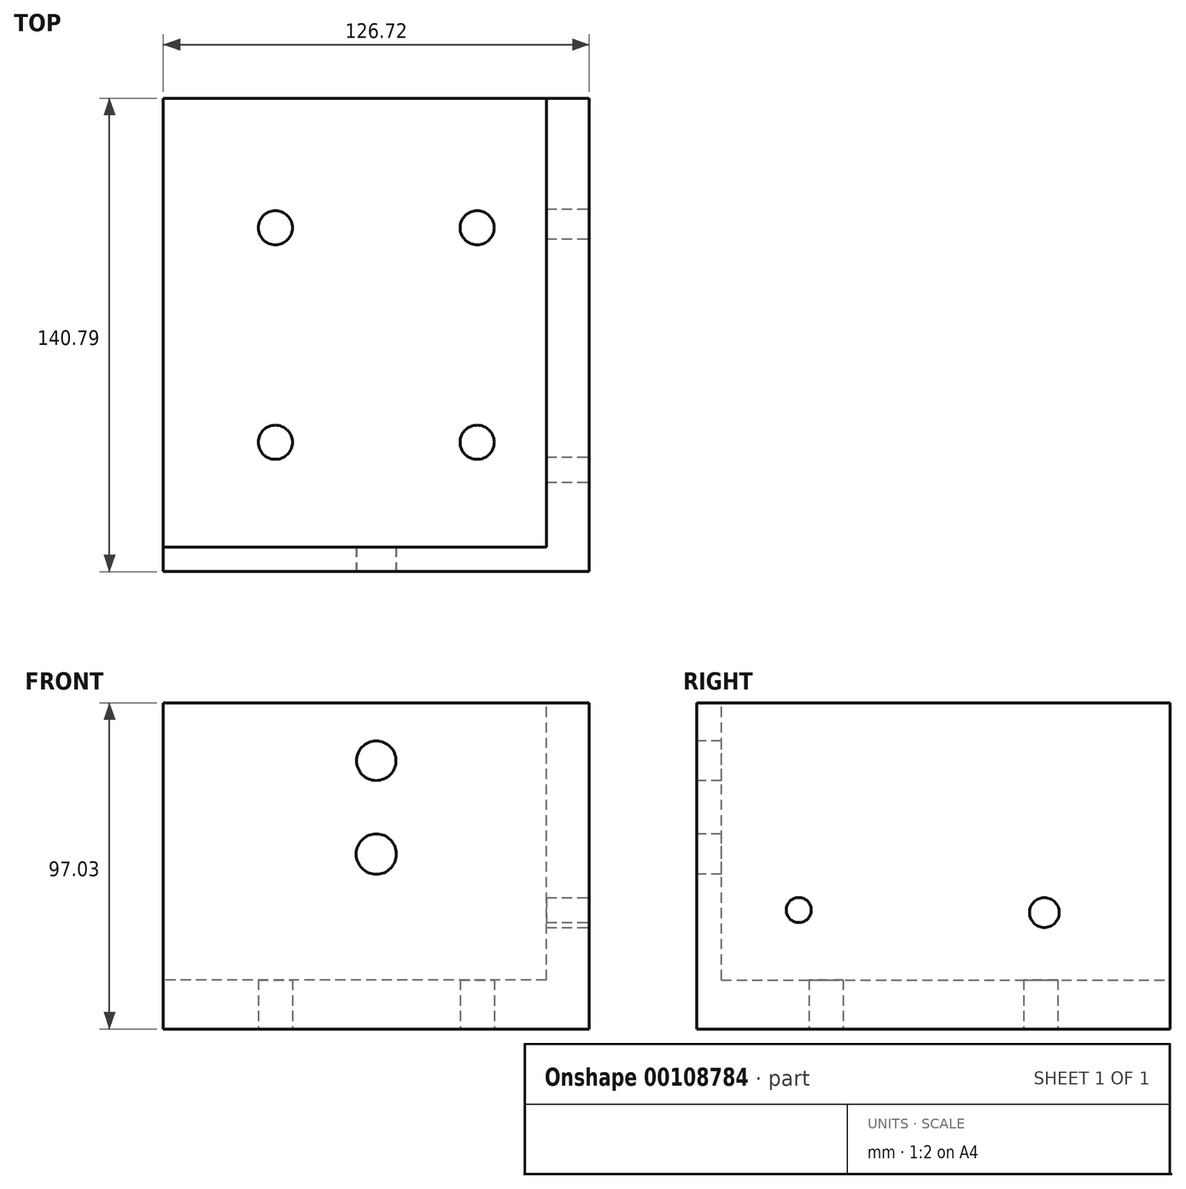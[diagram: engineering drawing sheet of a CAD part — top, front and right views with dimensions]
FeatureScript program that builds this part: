
annotation { "Feature Type Name" : "Feature", "Feature Type Description" : "" }
export const myFeature = defineFeature(function(context is Context, id is Id, definition is map)
    precondition{}
    {
        {
            var Q0;
            Q0=qCreatedBy(makeId("Front.planeOp"),FACE);
            var sketch = newSketch(context, id + "F0", { "sketchPlane" : qUnion([Q0])});
            skLineSegment(sketch, "E0.bottom", {"start": v(63.36, -7.3) * mm, "end": v(-63.36, -7.3) * mm});
            skLineSegment(sketch, "E0.top", {"start": v(63.36, 7.3) * mm, "end": v(-63.36, 7.3) * mm});
            skLineSegment(sketch, "E0.left", {"start": v(63.36, -7.3) * mm, "end": v(63.36, 7.3) * mm});
            skLineSegment(sketch, "E0.right", {"start": v(-63.36, -7.3) * mm, "end": v(-63.36, 7.3) * mm});
            skPoint(sketch, "E0.middle", {"position": v(0, 0) * mm});
            skLineSegment(sketch, "E1.bottom", {"start": v(-63.36, 7.3) * mm, "end": v(-50.64, 7.3) * mm});
            skLineSegment(sketch, "E1.top", {"start": v(-63.36, 89.74) * mm, "end": v(-50.64, 89.74) * mm});
            skLineSegment(sketch, "E1.left", {"start": v(-63.36, 7.3) * mm, "end": v(-63.36, 89.74) * mm});
            skLineSegment(sketch, "E1.right", {"start": v(-50.64, 7.3) * mm, "end": v(-50.64, 89.74) * mm});
            skLineSegment(sketch, "E2.MirrorCS", {"start": v(50.64, 7.3) * mm, "end": v(50.64, 89.74) * mm});
            skLineSegment(sketch, "E3.MirrorCS", {"start": v(63.36, 7.3) * mm, "end": v(50.64, 7.3) * mm});
            skLineSegment(sketch, "E4.MirrorCS", {"start": v(63.36, 7.3) * mm, "end": v(63.36, 89.74) * mm});
            skLineSegment(sketch, "E5.MirrorCS", {"start": v(63.36, 89.74) * mm, "end": v(50.64, 89.74) * mm});
            skSolve(sketch);
        }
        {
            var Q0;
            Q0=makeQuery(id+"F0.imprint","IMPRINT",FACE,{"disambiguationData":[TD([[makeQuery(id+"F0.imprint","IMPRINT",EDGE,{"derivedFrom":sQuery(id+"F0.wireOp",EDGE,"E1.bottom")}),1.0]])]});
            var Q1;
            Q1=makeQuery(id+"F0.imprint","IMPRINT",FACE,{"disambiguationData":[TD([[makeQuery(id+"F0.imprint","IMPRINT",EDGE,{"derivedFrom":sQuery(id+"F0.wireOp",EDGE,"E0.bottom")}),-1.0]])]});
            var Q2;
            Q2=makeQuery(id+"F0.imprint","IMPRINT",FACE,{"disambiguationData":[TD([[makeQuery(id+"F0.imprint","IMPRINT",EDGE,{"derivedFrom":sQuery(id+"F0.wireOp",EDGE,"E2.MirrorCS")}),-1.0]])]});
            extrude(context, id + "F1", {"entities" : qUnion([Q0, Q1, Q2]), "depth" : 140.79 * mm});
        }
        {
            var Q0;
            Q0=makeQuery(id+"F1.opExtrude","SWEPT_FACE",FACE,{"disambiguationData":[OSD([sQuery(id+"F0.wireOp",EDGE,"E0.left"),sQuery(id+"F0.wireOp",EDGE,"E4.MirrorCS")])]});
            var sketch = newSketch(context, id + "F2", { "sketchPlane" : qUnion([Q0])});
            skCircle(sketch, "E6", {"center": v(-110.43, 28.09) * mm, "radius": 3.72 * mm});
            skCircle(sketch, "E7", {"center": v(-37.36, 27.34) * mm, "radius": 4.43 * mm});
            skSolve(sketch);
        }
        {
            var Q0;
            Q0 = qSketchRegion(id + "F2", true);
            extrude(context, id + "F3", {"entities" : qUnion([Q0]), "operationType" : NewBodyOperationType.REMOVE, "oppositeDirection" : true, "depth" : 151.84 * mm});
        }
        {
            var Q0;
            Q0=makeQuery(id+"F1.opExtrude","CAP_FACE",FACE,{"disambiguationData":[OSD([sQuery(id+"F0.wireOp",EDGE,"E0.bottom"),sQuery(id+"F0.wireOp",EDGE,"E0.top"),sQuery(id+"F0.wireOp",EDGE,"E0.left"),sQuery(id+"F0.wireOp",EDGE,"E0.right"),sQuery(id+"F0.wireOp",EDGE,"E1.top"),sQuery(id+"F0.wireOp",EDGE,"E1.left"),sQuery(id+"F0.wireOp",EDGE,"E1.right"),sQuery(id+"F0.wireOp",EDGE,"E2.MirrorCS"),sQuery(id+"F0.wireOp",EDGE,"E4.MirrorCS"),sQuery(id+"F0.wireOp",EDGE,"E5.MirrorCS")])],"isStart":false});
            var sketch = newSketch(context, id + "F4", { "sketchPlane" : qUnion([Q0])});
            skLineSegment(sketch, "E8.bottom", {"start": v(-63.36, 89.74) * mm, "end": v(63.36, 89.74) * mm});
            skLineSegment(sketch, "E8.top", {"start": v(-63.36, -7.3) * mm, "end": v(63.36, -7.3) * mm});
            skLineSegment(sketch, "E8.left", {"start": v(-63.36, 89.74) * mm, "end": v(-63.36, -7.3) * mm});
            skLineSegment(sketch, "E8.right", {"start": v(63.36, 89.74) * mm, "end": v(63.36, -7.3) * mm});
            skSolve(sketch);
        }
        {
            var Q0;
            Q0 = qSketchRegion(id + "F4", true);
            extrude(context, id + "F5", {"entities" : qUnion([Q0]), "operationType" : NewBodyOperationType.ADD, "oppositeDirection" : true, "depth" : 7.33 * mm});
        }
        {
            var Q0;
            Q0=makeQuery(id+"F5.boolean.opBoolean","MERGE",FACE,{"derivedFrom":[makeQuery(id+"F1.opExtrude","CAP_FACE",FACE,{"disambiguationData":[OSD([sQuery(id+"F0.wireOp",EDGE,"E0.bottom"),sQuery(id+"F0.wireOp",EDGE,"E0.top"),sQuery(id+"F0.wireOp",EDGE,"E0.left"),sQuery(id+"F0.wireOp",EDGE,"E0.right"),sQuery(id+"F0.wireOp",EDGE,"E1.top"),sQuery(id+"F0.wireOp",EDGE,"E1.left"),sQuery(id+"F0.wireOp",EDGE,"E1.right"),sQuery(id+"F0.wireOp",EDGE,"E2.MirrorCS"),sQuery(id+"F0.wireOp",EDGE,"E4.MirrorCS"),sQuery(id+"F0.wireOp",EDGE,"E5.MirrorCS")])],"isStart":false}),makeQuery(id+"F5.opExtrude","CAP_FACE",FACE,{"disambiguationData":[OSD([sQuery(id+"F4.wireOp",EDGE,"E8.bottom"),sQuery(id+"F4.wireOp",EDGE,"E8.top"),sQuery(id+"F4.wireOp",EDGE,"E8.left"),sQuery(id+"F4.wireOp",EDGE,"E8.right")])],"isStart":true})]});
            var sketch = newSketch(context, id + "F6", { "sketchPlane" : qUnion([Q0])});
            skCircle(sketch, "E9", {"center": v(0, 44.73) * mm, "radius": 6 * mm});
            skCircle(sketch, "E10", {"center": v(0, 72.5) * mm, "radius": 5.88 * mm});
            skSolve(sketch);
        }
        {
            var Q0;
            Q0 = qSketchRegion(id + "F6", true);
            extrude(context, id + "F7", {"entities" : qUnion([Q0]), "operationType" : NewBodyOperationType.REMOVE, "oppositeDirection" : true, "depth" : 25.4 * mm});
        }
        {
            var Q0;
            Q0=makeQuery(id+"F1.opExtrude","SWEPT_FACE",FACE,{"disambiguationData":[OSD([sQuery(id+"F0.wireOp",EDGE,"E0.bottom")])]});
            var sketch = newSketch(context, id + "F8", { "sketchPlane" : qUnion([Q0])});
            skCircle(sketch, "E11", {"center": v(30.03, 102.3) * mm, "radius": 5.08 * mm});
            skCircle(sketch, "E12", {"center": v(30.03, 38.49) * mm, "radius": 5.08 * mm});
            skCircle(sketch, "E13", {"center": v(-30.03, 38.49) * mm, "radius": 5.08 * mm});
            skCircle(sketch, "E14", {"center": v(-30.03, 102.3) * mm, "radius": 5.08 * mm});
            skLineSegment(sketch, "E15", {"start": v(0, 140.79) * mm, "end": v(0, 0) * mm, "construction": true});
            skLineSegment(sketch, "E16", {"start": v(63.36, 70.4) * mm, "end": v(-63.36, 70.4) * mm, "construction": true});
            skSolve(sketch);
        }
        {
            var Q0;
            Q0 = qSketchRegion(id + "F8", true);
            extrude(context, id + "F9", {"entities" : qUnion([Q0]), "operationType" : NewBodyOperationType.REMOVE, "oppositeDirection" : true, "depth" : 25.4 * mm});
        }
    });
